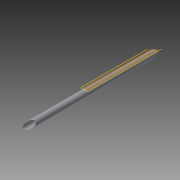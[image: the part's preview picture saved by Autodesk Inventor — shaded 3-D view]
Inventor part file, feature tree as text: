
AUTODESK INVENTOR PART (.ipt)
format: ipt  version: 2014 (Build 180170000, 170)  size: 112,640 bytes
history: native  units: in
note: dims shown in document units (in); Inventor stores cm internally (conversion verified against a paired STEP export)
features: extrude x3, plane x3, sketch x3
ambient origin geometry x8: Origin, YZ Plane, XZ Plane, XY Plane, X Axis, Y Axis, Z Axis, Center Point
bodies: Solid1 (feature_tree)
feature tree (9):
  extrude  "Extrusion1"  Depth=0.436in
  plane  "Work Plane1"
  extrude  "Extrusion2"  Depth=0.125in
  plane  "Work Plane3"
  extrude  "Extrusion3"  Depth=0.375in TaperAngle=0.0deg
  sketch  "Sketch1"  dims[d0=0.5in d1=0.436in]
  sketch  "Sketch2"  dims[d2=12.0in d3=0.0in d4=0.125in]
  plane  "Work Plane2"
  sketch  "Sketch3"  dims[d5=11.75in d6=1.0in d7=0.0in d10=0.375in d11=0.75in d12=0.5in d13=1.0in d14=0.0in]
